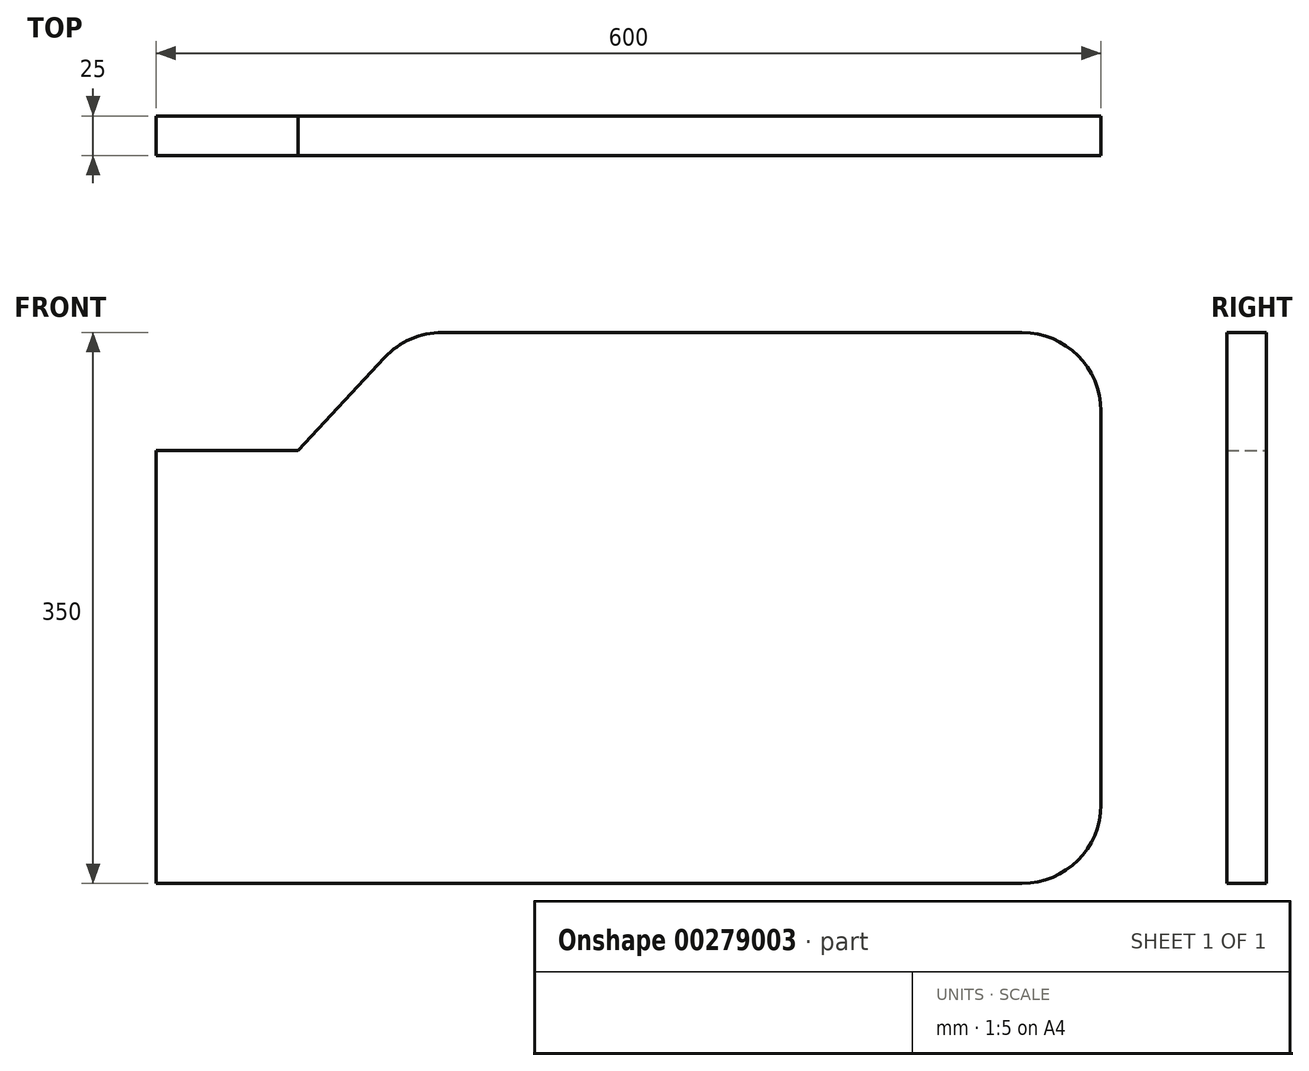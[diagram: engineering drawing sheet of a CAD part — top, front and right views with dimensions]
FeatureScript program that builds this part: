
annotation { "Feature Type Name" : "Feature", "Feature Type Description" : "" }
export const myFeature = defineFeature(function(context is Context, id is Id, definition is map)
    precondition{}
    {
        {
            var Q0;
            Q0=qCreatedBy(makeId("Front.planeOp"),FACE);
            var sketch = newSketch(context, id + "F0", { "sketchPlane" : qUnion([Q0])});
            skLineSegment(sketch, "E0.bottom", {"start": v(0, 0) * mm, "end": v(550, 0) * mm});
            skLineSegment(sketch, "E0.top", {"start": v(0, 350) * mm, "end": v(550, 350) * mm});
            skLineSegment(sketch, "E0.left", {"start": v(0, 0) * mm, "end": v(0, 350) * mm});
            skLineSegment(sketch, "E0.right", {"start": v(600, 50) * mm, "end": v(600, 300) * mm});
            skLineSegment(sketch, "E1", {"start": v(0, 275) * mm, "end": v(90, 275) * mm});
            skLineSegment(sketch, "E2", {"start": v(90, 275) * mm, "end": v(160, 350) * mm});
            skPoint(sketch, "E3.visualSharp", {"position": v(600, 350) * mm});
            skArc(sketch, "E3.filletArc", {"start": v(600, 300) * mm, "mid": v(585.36, 335.36) * mm, "end": v(550, 350) * mm});
            skPoint(sketch, "E4.visualSharp", {"position": v(600, 0) * mm});
            skArc(sketch, "E4.filletArc", {"start": v(550, 0) * mm, "mid": v(585.36, 14.64) * mm, "end": v(600, 50) * mm});
            skSolve(sketch);
        }
        {
            var Q0;
            {var subQ2=sQuery(id+"F0.wireOp",EDGE,"E0.bottom");Q0=makeQuery(id+"F0.imprint","IMPRINT",FACE,{"disambiguationData":[TD([[makeQuery(id+"F0.imprint","IMPRINT",EDGE,{"derivedFrom":subQ2}),1.0]])]});}
            extrude(context, id + "F1", {"entities" : qUnion([Q0]), "depth" : 25 * mm});
        }
        {
            var Q0;
            Q0=makeQuery(id+"F1.opExtrude","SWEPT_EDGE",EDGE,{"disambiguationData":[OSD([sQuery(id+"F0.wireOp",EDGE,"E0.top"),sQuery(id+"F0.wireOp",EDGE,"E2")])]});
            fillet(context, id + "F2", {"entities" : qUnion([Q0]), "radius" : 50 * mm, "tangentPropagation" : true, "allowEdgeOverflow" : false});
        }
    });
